# Revit family: Gas-Detectors_GSE-Generation-2-Standalone_Brasch
name_source: partatom
category: Generic Models
units: mm (PartAtom-declared; Revit-internal decimal feet)

## family parameters
Always vertical = Yes
Can host rebar = No
Cut with Voids When Loaded = No
Maintain Annotation Orientation = No
Part Type = Normal
Room Calculation Point = No
Round Connector Dimension = Use Diameter
Shared = No
Work Plane-Based = No

## types (5) — shared parameters
CAD Details = https://www.arcat.com
DEPTH = 2.90"
Default Elevation = 0.00"
HEIGHT = 10.50"
Input Voltage = 24 VAC, 120 VAC
Keynote = 28 42 15
Manufacturer = Brasch Environmental Technologies
Material = Gray
Product Page URL = https://www.arcat.com
Specification = https://www.arcat.com
URL = https://braschenvtech.com
WIDTH = 8.72"

## type names (no varying parameters)
- GSE2-CM, Carbon Monoxide Detector
- GSE2-ND, Nitrogen Dioxide Detector
- GSE2-OX, Oxygen Detector
- GSE2-NCM, Combination Detector, Nitrogen Dioxide and Carbon Monoxide
- GSE2, without any internal sensors

## geometry (parser evidence)
native form markers: Sweep x6
no freeform markers — native parametric forms only
